FCSTD DOCUMENT  (FreeCAD 0.18R15253 (Git))
Label: nesttest
License: All rights reserved
LicenseURL: http://en.wikipedia.org/wiki/All_rights_reserved
objects: Part::Part2DObjectPython×9
note: 9 computed .brp shape members not serialized (recipe doc carries the construction recipe); baked Part::Feature solids carry a one-line shape summary decoded from their .brp

FEATURE [Part::Part2DObjectPython] Wire  # Draft 2D object (typed FeaturePython)
  ChamferSize = 0
  Closed = true
  End = (-1.13284,1.21103,0)
  FilletRadius = 0
  Length = 2.67477
  MakeFace = true
  Placement = pos=(-1.78952,1.11,0) rot=(0,0,1;1.5708rad)
  Points = (4) [(0,0,0),(0.743275,0.0216488,0),(0.671113,-0.671113,0),(0.101028,-0.65668,0)]
  Start = (-1.78952,1.11,0)
  Subdivisions = 0
FEATURE [Part::Part2DObjectPython] Wire001  # Draft 2D object (typed FeaturePython)
  ChamferSize = 0
  Closed = true
  End = (-2.30734,2.26464,0)
  FilletRadius = 0
  Length = 3.53061
  MakeFace = true
  Placement = pos=(-2.46609,2.74813,0) rot=(0,0,-1;1.5708rad)
  Points = (8) [(0,0,0),(0.555652,-0.418543,0),(0.880384,-0.180407,0),(1.1979,-0.137109,0),(1.52263,0.194839,0),(0.974195,0.209272,0),(0.728842,0.0216489,0),(0.48349,0.158758,0)]
  Start = (-2.46609,2.74813,0)
  Subdivisions = 0
FEATURE [Part::Part2DObjectPython] Rectangle  # Draft 2D object (typed FeaturePython)
  ChamferSize = 0
  Columns = 1
  FilletRadius = 0
  Height = 2.13601
  Length = 3.637
  MakeFace = true
  Placement = pos=(-1.51,-1.89,0) rot=(0,0,1;0rad)
  Rows = 1
FEATURE [Part::Part2DObjectPython] Wire004  # Draft 2D object (typed FeaturePython)
  ChamferSize = 0
  Closed = true
  End = (-1.18527,3.10489,0)
  FilletRadius = 0
  Length = 2.67477
  MakeFace = true
  Placement = pos=(-0.528586,3.20592,0) rot=(0,0,-1;1.5708rad)
  Points = (4) [(0,0,0),(0.743275,0.0216488,0),(0.671113,-0.671113,0),(0.101028,-0.65668,0)]
  Start = (-0.528586,3.20592,0)
  Subdivisions = 0
FEATURE [Part::Part2DObjectPython] Wire005  # Draft 2D object (typed FeaturePython)
  ChamferSize = 0
  Closed = true
  End = (-1.74888,1.84679,0)
  FilletRadius = 0
  Length = 2.67477
  MakeFace = true
  Placement = pos=(-1.84991,2.50347,0) rot=(0,0,1;0rad)
  Points = (4) [(0,0,0),(0.743275,0.0216488,0),(0.671113,-0.671113,0),(0.101028,-0.65668,0)]
  Start = (-1.84991,2.50347,0)
  Subdivisions = 0
FEATURE [Part::Part2DObjectPython] Wire006  # Draft 2D object (typed FeaturePython)
  ChamferSize = 0
  Closed = true
  End = (-1.19795,2.60377,0)
  FilletRadius = 0
  Length = 2.67477
  MakeFace = true
  Placement = pos=(-1.85463,2.50274,0) rot=(0,0,1;1.5708rad)
  Points = (4) [(0,0,0),(0.743275,0.0216488,0),(0.671113,-0.671113,0),(0.101028,-0.65668,0)]
  Start = (-1.85463,2.50274,0)
  Subdivisions = 0
FEATURE [Part::Part2DObjectPython] Wire007  # Draft 2D object (typed FeaturePython)
  ChamferSize = 0
  Closed = true
  End = (-3.1888,2.02543,0)
  FilletRadius = 0
  Length = 5.76989
  MakeFace = true
  Placement = pos=(-3.07638,1.11,0) rot=(0,0,1;1.5708rad)
  Points = (6) [(0,0,0),(0.144541,-0.481803,0),(1.17239,-0.144541,0),(1.63813,-0.610284,0),(2.26447,0.433622,0),(0.915425,0.112421,0)]
  Start = (-3.07638,1.11,0)
  Subdivisions = 0
FEATURE [Part::Part2DObjectPython] Circle  # Draft 2D object (typed FeaturePython)
  FirstAngle = 0
  LastAngle = 0
  MakeFace = true
  Placement = pos=(-6.13754,0.823544,0) rot=(0,0,1;0rad)
  Radius = 0.498898
  Support = -> [Wire001]
FEATURE [Part::Part2DObjectPython] Polygon  # Draft 2D object (typed FeaturePython)
  ChamferSize = 0
  DrawMode = 0
  FacesNumber = 3
  FilletRadius = 0
  MakeFace = true
  Placement = pos=(-6.76873,3.83136,0) rot=(0,0,1;0rad)
  Radius = 0.0984093
